annotation { "Feature Type Name" : "Feature", "Feature Type Description" : "" }
export const myFeature = defineFeature(function(context is Context, id is Id, definition is map)
    precondition{}
    {
        {
            var Q0;
            Q0=qCreatedBy(makeId("Front.planeOp"),FACE);
            var sketch = newSketch(context, id + "F0", { "sketchPlane" : qUnion([Q0])});
            skLineSegment(sketch, "E0", {"start": v(0, 0) * mm, "end": v(-12192, 0) * mm});
            skLineSegment(sketch, "E1", {"start": v(-12192, 0) * mm, "end": v(-12192, 7315.2) * mm});
            skLineSegment(sketch, "E2", {"start": v(0, 0) * mm, "end": v(0, 7315.2) * mm});
            skLineSegment(sketch, "E3", {"start": v(0, 7315.2) * mm, "end": v(-12192, 7315.2) * mm});
            skLineSegment(sketch, "E4", {"start": v(-6096, 7315.2) * mm, "end": v(-6096, 10363.2) * mm});
            skLineSegment(sketch, "E5", {"start": v(-6096, 10363.2) * mm, "end": v(-12192, 7315.2) * mm});
            skLineSegment(sketch, "E6", {"start": v(-6096, 10363.2) * mm, "end": v(0, 7315.2) * mm});
            skLineSegment(sketch, "E7", {"start": v(-12192, 7315.2) * mm, "end": v(-13106.4, 7315.2) * mm});
            skLineSegment(sketch, "E8", {"start": v(-6096, 10363.2) * mm, "end": v(-6096, 10820.4) * mm});
            skLineSegment(sketch, "E9", {"start": v(-6096, 10820.4) * mm, "end": v(-13106.4, 7315.2) * mm});
            skLineSegment(sketch, "E10", {"start": v(0, 7315.2) * mm, "end": v(914.4, 7315.2) * mm});
            skLineSegment(sketch, "E11", {"start": v(914.4, 7315.2) * mm, "end": v(-6096, 10820.4) * mm});
            skLineSegment(sketch, "E12", {"start": v(-7010.4, 0) * mm, "end": v(-7010.4, 2133.6) * mm});
            skLineSegment(sketch, "E13", {"start": v(-7010.4, 2133.6) * mm, "end": v(-6096, 2133.6) * mm});
            skLineSegment(sketch, "E14", {"start": v(-6096, 2133.6) * mm, "end": v(-6096, 0) * mm});
            skCircle(sketch, "E15", {"center": v(-17365.38, 5866.75) * mm, "radius": 109.66 * mm});
            skLineSegment(sketch, "E16.bottom", {"start": v(-3657.6, 2743.2) * mm, "end": v(-1219.2, 2743.2) * mm});
            skLineSegment(sketch, "E16.top", {"start": v(-3657.6, 1219.2) * mm, "end": v(-1219.2, 1219.2) * mm});
            skLineSegment(sketch, "E16.left", {"start": v(-3657.6, 2743.2) * mm, "end": v(-3657.6, 1219.2) * mm});
            skLineSegment(sketch, "E16.right", {"start": v(-1219.2, 2743.2) * mm, "end": v(-1219.2, 1219.2) * mm});
            skText(sketch, "E17", { "text": "                YOUNG", "fontName": "OpenSans-Regular.ttf"});
            skLineSegment(sketch, "E18", {"start": v(-12192, 0) * mm, "end": v(-12192, -609.6) * mm});
            skLineSegment(sketch, "E19", {"start": v(-12192, -609.6) * mm, "end": v(0, -609.6) * mm});
            skLineSegment(sketch, "E20", {"start": v(0, 0) * mm, "end": v(0, -609.6) * mm});
            const initialGuessF0  = {"E17": [-18.08013, 12.8674, 1, 0, 1.50384]};
            skSetInitialGuess(sketch, initialGuessF0);
            skSolve(sketch);
        }
        {
            var Q0;
            {var subQ0=sQuery(id+"F0.wireOp",EDGE,"E18");Q0=makeQuery(id+"F0.imprint","IMPRINT",FACE,{"disambiguationData":[TD([[makeQuery(id+"F0.imprint","IMPRINT",EDGE,{"derivedFrom":subQ0}),1.0]])]});}
            extrude(context, id + "F1", {"entities" : qUnion([Q0]), "depth" : 1066.8 * mm, "offsetDistance" : 30.48 * mm});
        }
        {
            var Q0;
            Q0=makeQuery(id+"F1.opExtrude","SWEPT_FACE",FACE,{"disambiguationData":[OSD([sQuery(id+"F0.wireOp",EDGE,"E0")])]});
            var sketch = newSketch(context, id + "F2", { "sketchPlane" : qUnion([Q0])});
            skText(sketch, "E21", { "text": "Trevor Young", "fontName": "OpenSans-Regular.ttf"});
            const initialGuessF2  = {"E21": [-11.78744, -1.0668, 1, 0, 0.86018]};
            skSetInitialGuess(sketch, initialGuessF2);
            skSolve(sketch);
        }
        {
            var Q0;
            Q0 = qSketchRegion(id + "F2", true);
            extrude(context, id + "F3", {"entities" : qUnion([Q0]), "operationType" : NewBodyOperationType.ADD, "depth" : 30.48 * mm, "offsetDistance" : 30.48 * mm});
        }
        {
            var Q0;
            Q0=makeQuery(id+"F0.imprint","IMPRINT",FACE,{"disambiguationData":[TD([[makeQuery(id+"F0.imprint","IMPRINT",EDGE,{"derivedFrom":sQuery(id+"F0.wireOp",EDGE,"E5")}),-1.0]])]});
            var Q1;
            Q1=makeQuery(id+"F0.imprint","IMPRINT",FACE,{"disambiguationData":[TD([[makeQuery(id+"F0.imprint","IMPRINT",EDGE,{"derivedFrom":sQuery(id+"F0.wireOp",EDGE,"E6")}),1.0]])]});
            extrude(context, id + "F4", {"entities" : qUnion([Q0, Q1]), "endBound" : BoundingType.SYMMETRIC, "depth" : 7071.36 * mm, "offsetDistance" : 30.48 * mm});
        }
        {
            var Q0;
            {var subQ2=sQuery(id+"F0.wireOp",EDGE,"E4");Q0=makeQuery(id+"F0.imprint","IMPRINT",FACE,{"disambiguationData":[TD([[makeQuery(id+"F0.imprint","IMPRINT",EDGE,{"derivedFrom":subQ2}),1.0]])]});}
            var Q1;
            {var subQ2=sQuery(id+"F0.wireOp",EDGE,"E4");Q1=makeQuery(id+"F0.imprint","IMPRINT",FACE,{"disambiguationData":[TD([[makeQuery(id+"F0.imprint","IMPRINT",EDGE,{"derivedFrom":subQ2}),-1.0]])]});}
            extrude(context, id + "F5", {"entities" : qUnion([Q0, Q1]), "operationType" : NewBodyOperationType.ADD, "endBound" : BoundingType.SYMMETRIC, "depth" : 7254.24 * mm, "offsetDistance" : 30.48 * mm});
        }
        {
            var Q0;
            {var subQ2=sQuery(id+"F0.wireOp",EDGE,"E1");Q0=makeQuery(id+"F0.imprint","IMPRINT",FACE,{"disambiguationData":[TD([[makeQuery(id+"F0.imprint","IMPRINT",EDGE,{"derivedFrom":subQ2}),-1.0]])]});}
            extrude(context, id + "F6", {"entities" : qUnion([Q0]), "endBound" : BoundingType.SYMMETRIC, "depth" : 7071.36 * mm, "offsetDistance" : 30.48 * mm});
        }
        {
            var Q0;
            {var subQ0=sQuery(id+"F0.wireOp",EDGE,"E18");Q0=makeQuery(id+"F0.imprint","IMPRINT",FACE,{"disambiguationData":[TD([[makeQuery(id+"F0.imprint","IMPRINT",EDGE,{"derivedFrom":subQ0}),1.0]])]});}
            extrude(context, id + "F7", {"entities" : qUnion([Q0]), "endBound" : BoundingType.SYMMETRIC, "depth" : 10668 * mm, "offsetDistance" : 30.48 * mm});
        }
        {
            var Q0;
            {var subQ0=sQuery(id+"F0.wireOp",EDGE,"E12");Q0=makeQuery(id+"F0.imprint","IMPRINT",FACE,{"disambiguationData":[TD([[makeQuery(id+"F0.imprint","IMPRINT",EDGE,{"derivedFrom":subQ0}),-1.0]])]});}
            extrude(context, id + "F8", {"entities" : qUnion([Q0]), "endBound" : BoundingType.SYMMETRIC, "depth" : 6949.44 * mm, "offsetDistance" : 30.48 * mm});
        }
        {
            var Q0;
            Q0=makeQuery(id+"F0.imprint","IMPRINT",FACE,{"disambiguationData":[TD([[makeQuery(id+"F0.imprint","IMPRINT",EDGE,{"derivedFrom":sQuery(id+"F0.wireOp",EDGE,"E16.bottom")}),-1.0]])]});
            extrude(context, id + "F9", {"entities" : qUnion([Q0]), "operationType" : NewBodyOperationType.ADD, "endBound" : BoundingType.SYMMETRIC, "oppositeDirection" : true, "depth" : 7376.16 * mm, "offsetDistance" : 30.48 * mm});
        }
    });